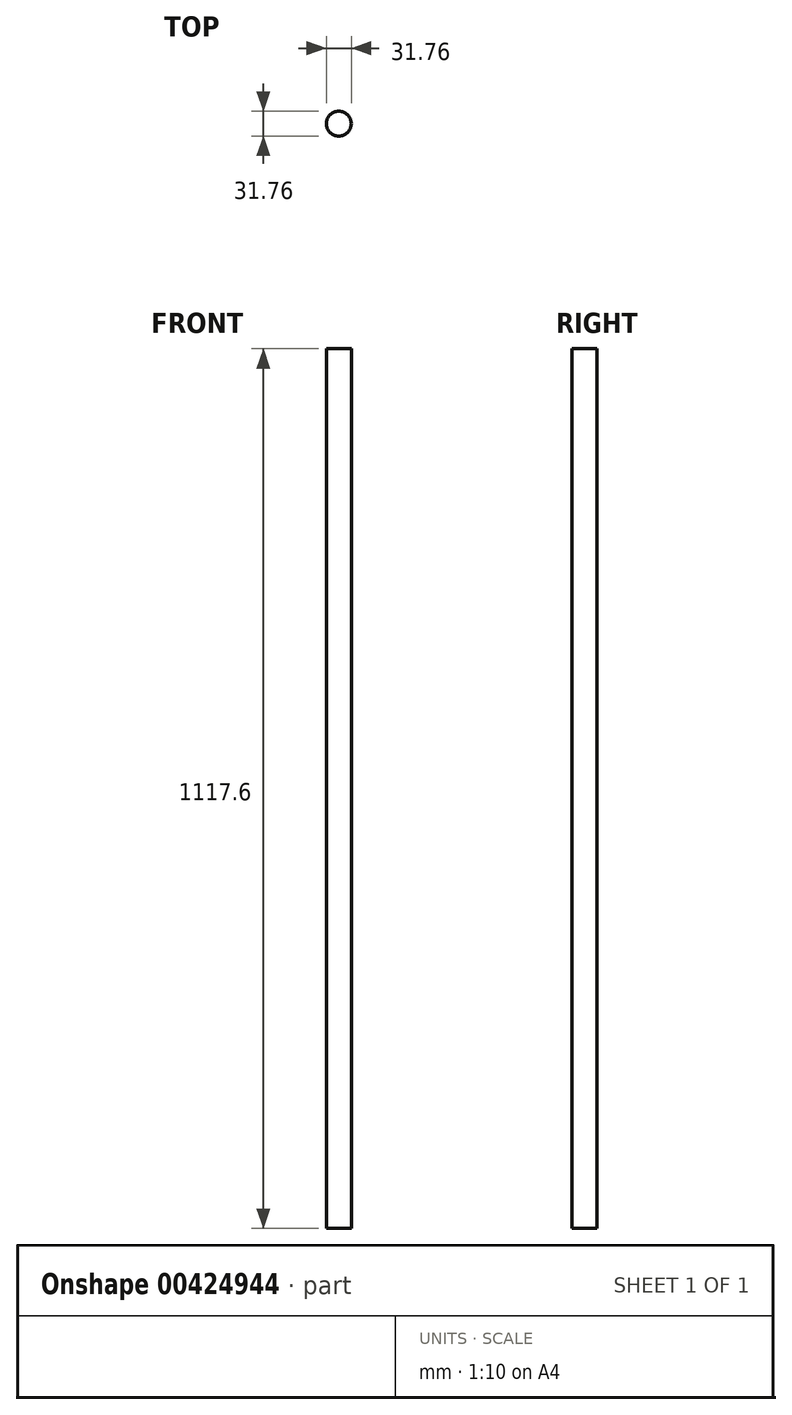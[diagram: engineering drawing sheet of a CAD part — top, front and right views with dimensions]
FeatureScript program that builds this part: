
annotation { "Feature Type Name" : "Feature", "Feature Type Description" : "" }
export const myFeature = defineFeature(function(context is Context, id is Id, definition is map)
    precondition{}
    {
        {
            var Q0;
            Q0=qCreatedBy(makeId("Top.planeOp"),FACE);
            var sketch = newSketch(context, id + "F0", { "sketchPlane" : qUnion([Q0])});
            skCircle(sketch, "E0", {"center": v(0, 0) * mm, "radius": 15.88 * mm});
            skSolve(sketch);
        }
        {
            var Q0;
            Q0=makeQuery(id+"F0.imprint","IMPRINT",FACE,{"disambiguationData":[TD([[makeQuery(id+"F0.imprint","IMPRINT",EDGE,{"derivedFrom":sQuery(id+"F0.wireOp",EDGE,"E0")}),1.0]])]});
            extrude(context, id + "F1", {"entities" : qUnion([Q0]), "depth" : 1117.6 * mm, "symmetric" : true});
        }
    });
